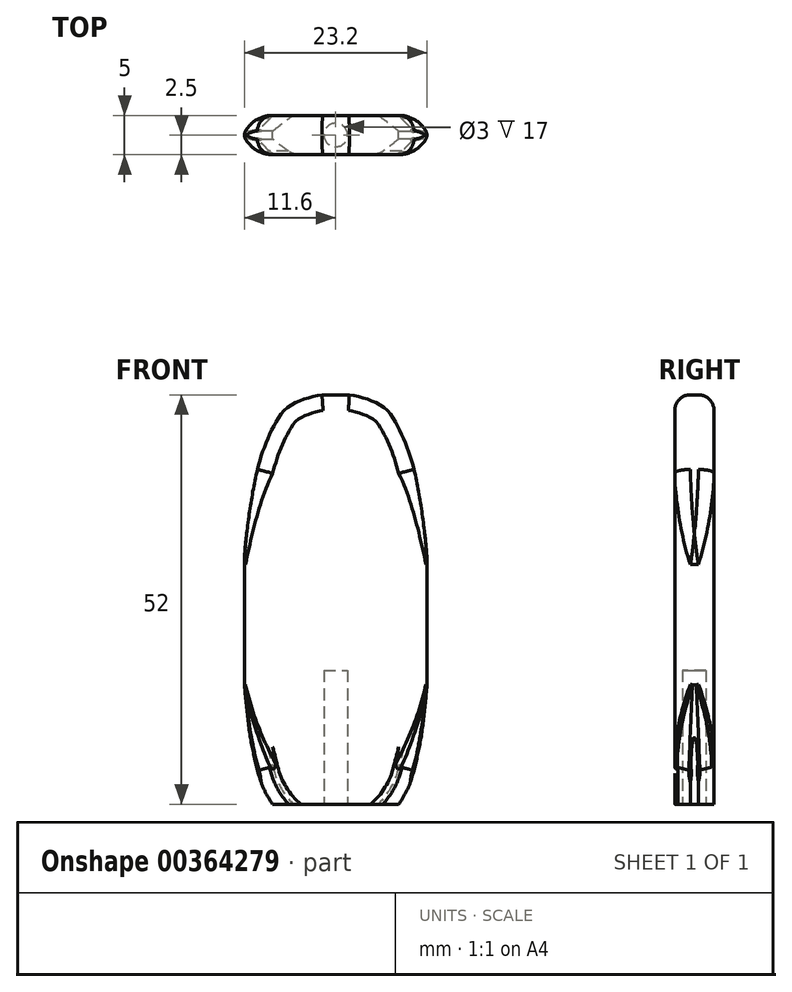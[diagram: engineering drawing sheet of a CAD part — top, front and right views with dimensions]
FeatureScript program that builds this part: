
annotation { "Feature Type Name" : "Feature", "Feature Type Description" : "" }
export const myFeature = defineFeature(function(context is Context, id is Id, definition is map)
    precondition{}
    {
        {
            var Q0;
            Q0=qCreatedBy(makeId("Front.planeOp"),FACE);
            var sketch = newSketch(context, id + "F0", { "sketchPlane" : qUnion([Q0])});
            skLineSegment(sketch, "E0.bottom", {"start": v(0, 0) * mm, "end": v(3.39, 0) * mm});
            skLineSegment(sketch, "E0.top", {"start": v(0, 55) * mm, "end": v(1.74, 55) * mm});
            skLineSegment(sketch, "E0.left", {"start": v(0, 0) * mm, "end": v(0, 55) * mm});
            skPoint(sketch, "E1.visualSharp", {"position": v(12, 0) * mm});
            skFitSpline(sketch, "E2", {"points": [v(12, 31) * mm, v(9.8, 46.06) * mm, v(7.52, 51.63) * mm, v(5.66, 53.7) * mm, v(1.74, 55) * mm, v(0, 55) * mm], "startDerivative": vector(-5.04, 48.72) * mm, "endDerivative": vector(-12.97, -1.27) * mm});
            skPoint(sketch, "E3.orphan", {"position": v(12, 55) * mm});
            skFitSpline(sketch, "E4", {"points": [v(12, 21.71) * mm, v(10.2, 8.37) * mm, v(8.58, 3.89) * mm, v(3.39, 0) * mm], "startDerivative": vector(-1.56, -40.07) * mm, "endDerivative": vector(-22.96, 0) * mm});
            skLineSegment(sketch, "E5", {"start": v(3.39, 0) * mm, "end": v(3.39, 0) * mm});
            skPoint(sketch, "E6.orphan", {"position": v(12, 7) * mm});
            skFitSpline(sketch, "E7", {"points": [v(12, 31) * mm, v(12, 21.71) * mm], "startDerivative": vector(0, -9.29) * mm, "endDerivative": vector(0, -9.29) * mm});
            skPoint(sketch, "E8.MirrorCS.start.orphan", {"position": v(0, 0) * mm});
            skSolve(sketch);
        }
        {
            var Q0;
            {var subQ1=sQuery(id+"F0.wireOp",EDGE,"E0.top");Q0=makeQuery(id+"F0.imprint","IMPRINT",FACE,{"disambiguationData":[TD([[makeQuery(id+"F0.imprint","IMPRINT",EDGE,{"derivedFrom":subQ1}),-1.0]])]});}
            extrude(context, id + "F1", {"entities" : qUnion([Q0]), "depth" : 5 * mm});
        }
        {
            var Q0;
            Q0=makeQuery(id+"F1.opExtrude","SWEPT_FACE",FACE,{"disambiguationData":[OSD([sQuery(id+"F0.wireOp",EDGE,"E0.bottom"),sQuery(id+"F0.wireOp",EDGE,"E8.MirrorCS")])]});
            var sketch = newSketch(context, id + "F2", { "sketchPlane" : qUnion([Q0])});
            skLineSegment(sketch, "E9", {"start": v(0, 0) * mm, "end": v(0, 5) * mm, "construction": true});
            skPoint(sketch, "E10", {"position": v(0, 2.5) * mm});
            skCircle(sketch, "E11", {"center": v(0, 2.5) * mm, "radius": 1.5 * mm});
            skSolve(sketch);
        }
        {
            var Q0;
            {var subQ0=sQuery(id+"F2.wireOp",EDGE,"E11");var subQ1=makeQuery(id+"F1.opExtrude","SWEPT_EDGE",EDGE,{"disambiguationData":[OSD([sQuery(id+"F0.wireOp",EDGE,"E0.left"),sQuery(id+"F0.wireOp",EDGE,"E0.bottom")])]});var subQ2=makeQuery(id+"F2.imprint","INTERSECT",VERTEX,{"disambiguationData":[OD(0.0)],"derivedFrom":[subQ1,subQ0]});Q0=makeQuery(id+"F2.imprint","IMPRINT",FACE,{"disambiguationData":[TD([[makeQuery(id+"F2.imprint","IMPRINT",EDGE,{"disambiguationData":[TD([[subQ2,-1.0]])],"derivedFrom":subQ0}),1.0]])]});}
            extrude(context, id + "F3", {"entities" : qUnion([Q0]), "operationType" : NewBodyOperationType.REMOVE, "oppositeDirection" : true, "depth" : 20 * mm});
        }
        {
            var Q0;
            Q0=makeQuery(id+"F1.opExtrude","CAP_EDGE",EDGE,{"disambiguationData":[OSD([sQuery(id+"F0.wireOp",EDGE,"E7")])],"isStart":false});
            var Q1;
            Q1=makeQuery(id+"F1.opExtrude","CAP_EDGE",EDGE,{"disambiguationData":[OSD([sQuery(id+"F0.wireOp",EDGE,"E7")])],"isStart":true});
            fillet(context, id + "F4", {"entities" : qUnion([Q0, Q1]), "radius" : 4 * mm, "tangentPropagation" : true, "allowEdgeOverflow" : false});
        }
        {
            var Q0;
            Q0=makeQuery(id+"F1.opExtrude","CAP_EDGE",EDGE,{"disambiguationData":[OSD([sQuery(id+"F0.wireOp",EDGE,"E0.bottom")])],"isStart":false});
            var Q1;
            Q1=makeQuery(id+"F1.opExtrude","CAP_EDGE",EDGE,{"disambiguationData":[OSD([sQuery(id+"F0.wireOp",EDGE,"E0.bottom")])],"isStart":true});
            chamfer(context, id + "F5", {"entities" : qUnion([Q0, Q1]), "width" : 2 * mm, "tangentPropagation" : true});
        }
        {
            var Q0;
            {var subQ0=sQuery(id+"F0.wireOp",EDGE,"E0.bottom");Q0=makeQuery(id+"F5.opChamfer","BLEND_EDGE",EDGE,{"blendedFrom":[makeQuery(id+"F1.opExtrude","CAP_EDGE",EDGE,{"disambiguationData":[OSD([subQ0])],"isStart":false}),makeQuery(id+"F1.opExtrude","CAP_FACE",FACE,{"disambiguationData":[OSD([sQuery(id+"F0.wireOp",EDGE,"E0.top"),sQuery(id+"F0.wireOp",EDGE,"E0.left"),sQuery(id+"F0.wireOp",EDGE,"E2"),sQuery(id+"F0.wireOp",EDGE,"E4"),subQ0,sQuery(id+"F0.wireOp",EDGE,"E7")])],"isStart":false})],"blendedInto":[makeQuery(id+"F1.opExtrude","CAP_FACE",FACE,{"disambiguationData":[OSD([sQuery(id+"F0.wireOp",EDGE,"E0.top"),sQuery(id+"F0.wireOp",EDGE,"E0.left"),sQuery(id+"F0.wireOp",EDGE,"E2"),sQuery(id+"F0.wireOp",EDGE,"E4"),subQ0,sQuery(id+"F0.wireOp",EDGE,"E7")])],"isStart":false})]});}
            var Q1;
            {var subQ0=sQuery(id+"F0.wireOp",EDGE,"E0.bottom");Q1=makeQuery(id+"F5.opChamfer","BLEND_EDGE",EDGE,{"blendedFrom":[makeQuery(id+"F1.opExtrude","CAP_EDGE",EDGE,{"disambiguationData":[OSD([subQ0])],"isStart":true}),makeQuery(id+"F1.opExtrude","CAP_FACE",FACE,{"disambiguationData":[OSD([sQuery(id+"F0.wireOp",EDGE,"E0.top"),sQuery(id+"F0.wireOp",EDGE,"E0.left"),sQuery(id+"F0.wireOp",EDGE,"E2"),sQuery(id+"F0.wireOp",EDGE,"E4"),subQ0,sQuery(id+"F0.wireOp",EDGE,"E7")])],"isStart":true})],"blendedInto":[makeQuery(id+"F1.opExtrude","CAP_FACE",FACE,{"disambiguationData":[OSD([sQuery(id+"F0.wireOp",EDGE,"E0.top"),sQuery(id+"F0.wireOp",EDGE,"E0.left"),sQuery(id+"F0.wireOp",EDGE,"E2"),sQuery(id+"F0.wireOp",EDGE,"E4"),subQ0,sQuery(id+"F0.wireOp",EDGE,"E7")])],"isStart":true})]});}
            fillet(context, id + "F6", {"entities" : qUnion([Q0, Q1]), "radius" : 1.5 * mm, "tangentPropagation" : true, "allowEdgeOverflow" : false});
        }
        {
            var Q0;
            {var subQ0=sQuery(id+"F0.wireOp",EDGE,"E7");var subQ1=makeQuery(id+"F1.opExtrude","CAP_EDGE",EDGE,{"disambiguationData":[OSD([subQ0])],"isStart":false});Q0=makeQuery(id+"F5.opChamfer","BLEND_EDGE",EDGE,{"blendedFrom":[makeQuery(id+"F4.opFillet","BLEND_EDGE",EDGE,{"blendedFrom":[subQ1,makeQuery(id+"F1.opExtrude","SWEPT_FACE",FACE,{"disambiguationData":[OSD([sQuery(id+"F0.wireOp",EDGE,"E4")])]})],"blendedInto":[makeQuery(id+"F1.opExtrude","SWEPT_FACE",FACE,{"disambiguationData":[OSD([sQuery(id+"F0.wireOp",EDGE,"E4")])]})]}),makeQuery(id+"F4.opFillet","BLEND_FACE",FACE,{"disambiguationData":[OSD([subQ0]),TDD([subQ1])]})],"blendedInto":[makeQuery(id+"F4.opFillet","BLEND_FACE",FACE,{"disambiguationData":[OSD([subQ0]),TDD([subQ1])]})]});}
            var Q1;
            {var subQ0=sQuery(id+"F0.wireOp",EDGE,"E7");var subQ1=makeQuery(id+"F1.opExtrude","CAP_EDGE",EDGE,{"disambiguationData":[OSD([subQ0])],"isStart":true});Q1=makeQuery(id+"F5.opChamfer","BLEND_EDGE",EDGE,{"blendedFrom":[makeQuery(id+"F4.opFillet","BLEND_EDGE",EDGE,{"blendedFrom":[subQ1,makeQuery(id+"F1.opExtrude","SWEPT_FACE",FACE,{"disambiguationData":[OSD([sQuery(id+"F0.wireOp",EDGE,"E4")])]})],"blendedInto":[makeQuery(id+"F1.opExtrude","SWEPT_FACE",FACE,{"disambiguationData":[OSD([sQuery(id+"F0.wireOp",EDGE,"E4")])]})]}),makeQuery(id+"F4.opFillet","BLEND_FACE",FACE,{"disambiguationData":[OSD([subQ0]),TDD([subQ1])]})],"blendedInto":[makeQuery(id+"F4.opFillet","BLEND_FACE",FACE,{"disambiguationData":[OSD([subQ0]),TDD([subQ1])]})]});}
            fillet(context, id + "F7", {"entities" : qUnion([Q0, Q1]), "radius" : 1 * mm, "tangentPropagation" : true, "allowEdgeOverflow" : false});
        }
        {
            var Q0;
            Q0=makeQuery(id+"F1.opExtrude","CAP_EDGE",EDGE,{"disambiguationData":[OSD([sQuery(id+"F0.wireOp",EDGE,"E0.top")])],"isStart":false});
            var Q1;
            Q1=makeQuery(id+"F1.opExtrude","CAP_EDGE",EDGE,{"disambiguationData":[OSD([sQuery(id+"F0.wireOp",EDGE,"E2")])],"isStart":false});
            var Q2;
            Q2=makeQuery(id+"F1.opExtrude","CAP_EDGE",EDGE,{"disambiguationData":[OSD([sQuery(id+"F0.wireOp",EDGE,"E0.top")])],"isStart":true});
            var Q3;
            Q3=makeQuery(id+"F1.opExtrude","CAP_EDGE",EDGE,{"disambiguationData":[OSD([sQuery(id+"F0.wireOp",EDGE,"E2")])],"isStart":true});
            fillet(context, id + "F8", {"entities" : qUnion([Q0, Q1, Q2, Q3]), "radius" : 2 * mm, "tangentPropagation" : true, "allowEdgeOverflow" : false});
        }
        {
            var Q0;
            {var subQ0=sQuery(id+"F0.wireOp",EDGE,"E7");Q0=makeQuery(id+"F4.opFillet","BLEND_EDGE",EDGE,{"blendedFrom":[makeQuery(id+"F1.opExtrude","CAP_EDGE",EDGE,{"disambiguationData":[OSD([subQ0])],"isStart":true}),makeQuery(id+"F1.opExtrude","CAP_EDGE",EDGE,{"disambiguationData":[OSD([subQ0])],"isStart":false})],"blendedInto":[]});}
            fillet(context, id + "F9", {"entities" : qUnion([Q0]), "radius" : 1 * mm, "tangentPropagation" : true, "allowEdgeOverflow" : false});
        }
        {
            var Q0;
            Q0=makeQuery(id+"F1.opExtrude","SWEPT_BODY",BODY,{"disambiguationData":[OSD([sQuery(id+"F0.wireOp",EDGE,"E0.top"),sQuery(id+"F0.wireOp",EDGE,"E0.left"),sQuery(id+"F0.wireOp",EDGE,"E2"),sQuery(id+"F0.wireOp",EDGE,"E4"),sQuery(id+"F0.wireOp",EDGE,"E0.bottom"),sQuery(id+"F0.wireOp",EDGE,"E7")])]});
            var Q1;
            Q1=makeQuery(id+"F1.opExtrude","SWEPT_FACE",FACE,{"disambiguationData":[OSD([sQuery(id+"F0.wireOp",EDGE,"E0.left")])]});
            mirror(context, id + "F10", {"operationType" : NewBodyOperationType.ADD, "entities" : qUnion([Q0]), "mirrorPlane" : qUnion([Q1])});
        }
        {
            var Q0;
            Q0=qCreatedBy(makeId("Top.planeOp"),FACE);
            var sketch = newSketch(context, id + "F11", { "sketchPlane" : qUnion([Q0])});
            skLineSegment(sketch, "E12.bottom", {"start": v(-20, -10) * mm, "end": v(20, -10) * mm});
            skLineSegment(sketch, "E12.top", {"start": v(-20, 10) * mm, "end": v(20, 10) * mm});
            skLineSegment(sketch, "E12.left", {"start": v(-20, -10) * mm, "end": v(-20, 10) * mm});
            skLineSegment(sketch, "E12.right", {"start": v(20, -10) * mm, "end": v(20, 10) * mm});
            skPoint(sketch, "E12.middle", {"position": v(0, 0) * mm});
            skSolve(sketch);
        }
        {
            var Q0;
            Q0=makeQuery(id+"F11.imprint","IMPRINT",FACE,{"disambiguationData":[TD([[makeQuery(id+"F11.imprint","IMPRINT",EDGE,{"derivedFrom":sQuery(id+"F11.wireOp",EDGE,"E12.bottom")}),1.0]])]});
            extrude(context, id + "F12", {"entities" : qUnion([Q0]), "operationType" : NewBodyOperationType.REMOVE, "depth" : 3 * mm});
        }
    });
